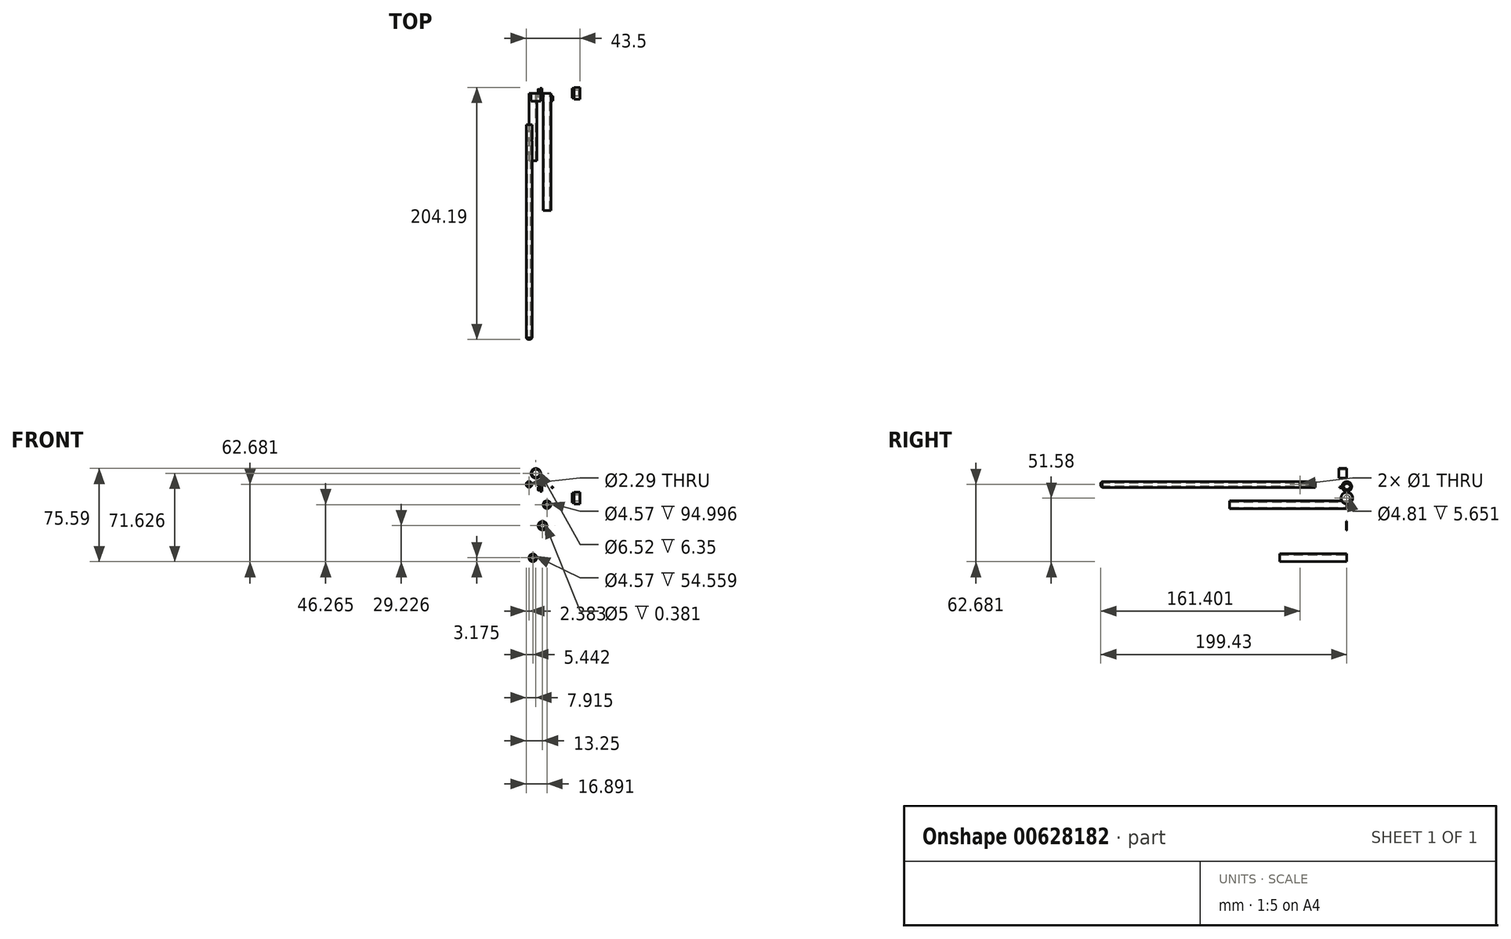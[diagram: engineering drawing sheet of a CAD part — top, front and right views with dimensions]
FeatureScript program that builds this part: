
annotation { "Feature Type Name" : "Feature", "Feature Type Description" : "" }
export const myFeature = defineFeature(function(context is Context, id is Id, definition is map)
    precondition{}
    {
        {
            var Q0;
            Q0=qCreatedBy(makeId("Front.planeOp"),FACE);
            var sketch = newSketch(context, id + "F0", { "sketchPlane" : qUnion([Q0])});
            skCircle(sketch, "E0", {"center": v(-51.91, 52.53) * mm, "radius": 3.97 * mm});
            skCircle(sketch, "E1", {"center": v(-51.91, 52.53) * mm, "radius": 3.26 * mm});
            skSolve(sketch);
        }
        {
            var Q0;
            Q0=makeQuery(id+"F0.imprint","IMPRINT",FACE,{"disambiguationData":[TD([[makeQuery(id+"F0.imprint","IMPRINT",EDGE,{"derivedFrom":sQuery(id+"F0.wireOp",EDGE,"E0")}),1.0]])]});
            extrude(context, id + "F1", {"entities" : qUnion([Q0]), "depth" : 6.35 * mm});
        }
        {
            var Q0;
            Q0=qCreatedBy(makeId("Front.planeOp"),FACE);
            var sketch = newSketch(context, id + "F2", { "sketchPlane" : qUnion([Q0])});
            skCircle(sketch, "E2", {"center": v(-64.02, 41.15) * mm, "radius": 0.5 * mm});
            skSolve(sketch);
        }
        {
            var Q0;
            Q0=makeQuery(id+"F2.imprint","IMPRINT",FACE,{"disambiguationData":[TD([[makeQuery(id+"F2.imprint","IMPRINT",EDGE,{"derivedFrom":sQuery(id+"F2.wireOp",EDGE,"E2")}),1.0]])]});
            extrude(context, id + "F3", {"entities" : qUnion([Q0]), "depth" : 6 * mm});
        }
        {
            var Q0;
            Q0=qCreatedBy(makeId("Front.planeOp"),FACE);
            var sketch = newSketch(context, id + "F4", { "sketchPlane" : qUnion([Q0])});
            skCircle(sketch, "E3", {"center": v(-57.45, 43.58) * mm, "radius": 1.14 * mm});
            skCircle(sketch, "E4", {"center": v(-57.45, 43.58) * mm, "radius": 2.38 * mm});
            skSolve(sketch);
        }
        {
            var Q0;
            Q0=makeQuery(id+"F4.imprint","IMPRINT",FACE,{"disambiguationData":[TD([[makeQuery(id+"F4.imprint","IMPRINT",EDGE,{"derivedFrom":sQuery(id+"F4.wireOp",EDGE,"E3")}),-1.0]])]});
            extrude(context, id + "F5", {"entities" : qUnion([Q0]), "depth" : 169.06 * mm + 5 * mm});
        }
        {
            var Q0;
            Q0=qCreatedBy(makeId("Front.planeOp"),FACE);
            var sketch = newSketch(context, id + "F6", { "sketchPlane" : qUnion([Q0])});
            skLineSegment(sketch, "E5.left", {"start": v(-50.2, 41.88) * mm, "end": v(-50.2, 45.11) * mm});
            skLineSegment(sketch, "E6.bottom", {"start": v(-48.6, 45.85) * mm, "end": v(-47.02, 45.85) * mm});
            skLineSegment(sketch, "E6.top", {"start": v(-48.6, 45.85) * mm, "end": v(-47.02, 45.85) * mm});
            skLineSegment(sketch, "E6.left", {"start": v(-50.2, 45.85) * mm, "end": v(-50.2, 45.85) * mm});
            skLineSegment(sketch, "E6.right", {"start": v(-47.02, 45.85) * mm, "end": v(-47.02, 45.85) * mm});
            skLineSegment(sketch, "E7.top", {"start": v(-47.02, 44.38) * mm, "end": v(-47.02, 44.38) * mm});
            skLineSegment(sketch, "E7.left", {"start": v(-47.02, 45.85) * mm, "end": v(-47.02, 44.38) * mm});
            skLineSegment(sketch, "E7.right", {"start": v(-47.02, 45.85) * mm, "end": v(-47.02, 44.38) * mm});
            skLineSegment(sketch, "E8.right", {"start": v(-44.58, 44.38) * mm, "end": v(-44.58, 44.38) * mm});
            skLineSegment(sketch, "E9.bottom", {"start": v(-50.2, 41.88) * mm, "end": v(-47.02, 41.88) * mm});
            skLineSegment(sketch, "E9.left", {"start": v(-50.2, 41.88) * mm, "end": v(-50.2, 41.86) * mm});
            skLineSegment(sketch, "E10", {"start": v(-47.02, 44.38) * mm, "end": v(-47.02, 41.88) * mm});
            skLineSegment(sketch, "E11", {"start": v(-48.6, 45.85) * mm, "end": v(-48.6, 45.11) * mm});
            skPoint(sketch, "E11.endSnap0", {"position": v(-47.02, 45.11) * mm});
            skLineSegment(sketch, "E12", {"start": v(-48.6, 45.11) * mm, "end": v(-50.2, 45.11) * mm});
            skSolve(sketch);
        }
        {
            var Q0;
            Q0=makeQuery(id+"F3.opExtrude","SWEPT_BODY",BODY,{"disambiguationData":[OSD([sQuery(id+"F2.wireOp",EDGE,"E2")])]});
            var Q1;
            Q1=qCreatedBy(makeId("Right.planeOp"),FACE);
            transform(context, id + "F7", {"entities" : qUnion([Q0]), "transformType" : TransformType.TRANSLATION_DISTANCE, "transformDirection" : qUnion([Q1]), "distance" : 25.4 * mm, "makeCopy" : false});
        }
        {
            var Q0;
            Q0=makeQuery(id+"F5.opExtrude","SWEPT_BODY",BODY,{"disambiguationData":[OSD([sQuery(id+"F4.wireOp",EDGE,"E3"),sQuery(id+"F4.wireOp",EDGE,"E4")])]});
            transform(context, id + "F8", {"entities" : qUnion([Q0]), "transformType" : TransformType.TRANSLATION_3D, "dx" : 0 * mm, "dy" : -25.4 * mm, "dz" : 0 * mm, "makeCopy" : false});
        }
        {
            var Q0;
            Q0=makeQuery(id+"F6.imprint","IMPRINT",FACE,{"disambiguationData":[TD([[makeQuery(id+"F6.imprint","IMPRINT",EDGE,{"derivedFrom":sQuery(id+"F6.wireOp",EDGE,"E5.left")}),-1.0]])]});
            var Q1;
            Q1=sQuery(id+"F6.wireOp",EDGE,"E9.bottom");
            revolve(context, id + "F9", {"entities" : qUnion([Q0]), "axis" : qUnion([Q1]), "revolveType" : RevolveType.FULL});
        }
        {
            var Q0;
            Q0=makeQuery(id+"F9.opRevolve","SWEPT_FACE",FACE,{"disambiguationData":[OSD([sQuery(id+"F6.wireOp",EDGE,"E5.left")])]});
            var sketch = newSketch(context, id + "F10", { "sketchPlane" : qUnion([Q0])});
            skLineSegment(sketch, "E13", {"start": v(0, 47.63) * mm, "end": v(0, 37.86) * mm, "construction": true});
            skPoint(sketch, "E14.visualSharp", {"position": v(5.58, 45.21) * mm});
            skCircle(sketch, "E15.0.0", {"center": v(0, 41.88) * mm, "radius": 3.97 * mm});
            skLineSegment(sketch, "E16", {"start": v(-3.97, 41.88) * mm, "end": v(3.97, 41.88) * mm, "construction": true});
            skLineSegment(sketch, "E17", {"start": v(-0.6, 45.4) * mm, "end": v(0, 45.4) * mm});
            skLineSegment(sketch, "E18", {"start": v(-0.6, 45.4) * mm, "end": v(-0.6, 41.88) * mm});
            skLineSegment(sketch, "E19.MirrorCS", {"start": v(0.6, 45.4) * mm, "end": v(0.6, 41.88) * mm});
            skLineSegment(sketch, "E20.MirrorCS", {"start": v(0.6, 45.4) * mm, "end": v(0, 45.4) * mm});
            skLineSegment(sketch, "E21.MirrorCS", {"start": v(-0.6, 38.36) * mm, "end": v(-0.6, 41.88) * mm});
            skLineSegment(sketch, "E22.MirrorCS", {"start": v(0.6, 38.36) * mm, "end": v(0.6, 41.88) * mm});
            skLineSegment(sketch, "E23.MirrorCS", {"start": v(0.6, 38.36) * mm, "end": v(0, 38.36) * mm});
            skLineSegment(sketch, "E24.MirrorCS", {"start": v(-0.6, 38.36) * mm, "end": v(0, 38.36) * mm});
            skSolve(sketch);
        }
        {
            var Q0;
            {var subQ6=sQuery(id+"F10.wireOp",EDGE,"E21.MirrorCS");var subQ8=sQuery(id+"F10.wireOp",EDGE,"E18");var subQ9=makeQuery(id+"F10.imprint","INTERSECT",VERTEX,{"derivedFrom":[subQ8,subQ6]});Q0=makeQuery(id+"F10.imprint","IMPRINT",FACE,{"disambiguationData":[TD([[makeQuery(id+"F10.imprint","IMPRINT",EDGE,{"disambiguationData":[TD([[subQ9,1.0]])],"derivedFrom":subQ8}),1.0]])]});}
            var Q1;
            {var subQ5=sQuery(id+"F10.wireOp",EDGE,"E17");Q1=makeQuery(id+"F10.imprint","IMPRINT",FACE,{"disambiguationData":[TD([[makeQuery(id+"F10.imprint","IMPRINT",EDGE,{"derivedFrom":subQ5}),-1.0]])]});}
            var Q2;
            {var subQ0=sQuery(id+"F10.wireOp",EDGE,"E23.MirrorCS");Q2=makeQuery(id+"F10.imprint","IMPRINT",FACE,{"disambiguationData":[TD([[makeQuery(id+"F10.imprint","IMPRINT",EDGE,{"derivedFrom":subQ0}),-1.0]])]});}
            var Q3;
            Q3=sQuery(id+"F10.wireOp",EDGE,"2e8Hojdz-Ffpt-K0kl-VxPV-xugqv5EDbXKW");
            var Q4;
            Q4=sQuery(id+"F10.wireOp",EDGE,"6102cfec-8d7d-461d-8d47-9e56d8466cac");
            var Q5;
            Q5=sQuery(id+"F10.wireOp",EDGE,"agnaYoGs-KZ4Y-nJwN-nZj2-FF0KZsyTTmNx");
            var Q6;
            Q6=sQuery(id+"F10.wireOp",EDGE,"wewaszXl-kRDa-fHt1-iyU0-6mpRW7kojRDx");
            var Q7;
            Q7=sQuery(id+"F10.wireOp",EDGE,"H97231xH-nEsN-Zyv9-0dKe-9AKgBbp31TFk");
            var Q8;
            Q8=sQuery(id+"F10.wireOp",EDGE,"9b957f26-6c3a-4b0b-aece-a967bed79c3a0.MirrorCS");
            extrude(context, id + "F11", {"entities" : qUnion([Q0, Q1, Q2]), "operationType" : NewBodyOperationType.REMOVE, "surfaceEntities" : qUnion([Q3, Q4, Q5, Q6, Q7, Q8]), "oppositeDirection" : true, "depth" : 1.59 * mm});
        }
        {
            var Q0;
            Q0=makeQuery(id+"F11.boolean.opBoolean","SPLIT",FACE,{"disambiguationData":[TD([makeQuery(id+"F11.opExtrude","SWEPT_FACE",FACE,{"disambiguationData":[OSD([sQuery(id+"F10.wireOp",EDGE,"E19.MirrorCS"),sQuery(id+"F10.wireOp",EDGE,"E22.MirrorCS")])]})])],"derivedFrom":makeQuery(id+"F9.opRevolve","SWEPT_FACE",FACE,{"disambiguationData":[OSD([sQuery(id+"F6.wireOp",EDGE,"E5.left")])]})});
            var sketch = newSketch(context, id + "F12", { "sketchPlane" : qUnion([Q0])});
            skCircle(sketch, "E25", {"center": v(0, 41.83) * mm, "radius": 2.5 * mm});
            skSolve(sketch);
        }
        {
            var Q0;
            {var subQ0=sQuery(id+"F12.wireOp",EDGE,"E25");var subQ1=makeQuery(id+"F11.boolean.opBoolean","COPY",EDGE,{"derivedFrom":makeQuery(id+"F11.opExtrude","CAP_EDGE",EDGE,{"disambiguationData":[OSD([sQuery(id+"F10.wireOp",EDGE,"agnaYoGs-KZ4Y-nJwN-nZj2-FF0KZsyTTmNx"),sQuery(id+"F10.wireOp",EDGE,"wewaszXl-kRDa-fHt1-iyU0-6mpRW7kojRDx")])],"isStart":true})});var subQ2=makeQuery(id+"F12.imprint","INTERSECT",VERTEX,{"disambiguationData":[OD(0.0)],"derivedFrom":[subQ1,subQ0]});Q0=makeQuery(id+"F12.imprint","IMPRINT",FACE,{"disambiguationData":[TD([[makeQuery(id+"F12.imprint","IMPRINT",EDGE,{"disambiguationData":[TD([[subQ2,1.0]])],"derivedFrom":subQ0}),1.0]])]});}
            var Q1;
            {var subQ0=sQuery(id+"F12.wireOp",EDGE,"E25");var subQ1=makeQuery(id+"F11.boolean.opBoolean","COPY",EDGE,{"derivedFrom":makeQuery(id+"F11.opExtrude","CAP_EDGE",EDGE,{"disambiguationData":[OSD([sQuery(id+"F10.wireOp",EDGE,"2e8Hojdz-Ffpt-K0kl-VxPV-xugqv5EDbXKW"),sQuery(id+"F10.wireOp",EDGE,"H97231xH-nEsN-Zyv9-0dKe-9AKgBbp31TFk")])],"isStart":true})});var subQ2=makeQuery(id+"F12.imprint","INTERSECT",VERTEX,{"disambiguationData":[OD(0.0)],"derivedFrom":[subQ1,subQ0]});Q1=makeQuery(id+"F12.imprint","IMPRINT",FACE,{"disambiguationData":[TD([[makeQuery(id+"F12.imprint","IMPRINT",EDGE,{"disambiguationData":[TD([[subQ2,1.0]])],"derivedFrom":subQ0}),1.0]])]});}
            var Q2;
            {var subQ0=sQuery(id+"F12.wireOp",EDGE,"E25");var subQ1=makeQuery(id+"F11.boolean.opBoolean","COPY",EDGE,{"derivedFrom":makeQuery(id+"F11.opExtrude","CAP_EDGE",EDGE,{"disambiguationData":[OSD([sQuery(id+"F10.wireOp",EDGE,"2e8Hojdz-Ffpt-K0kl-VxPV-xugqv5EDbXKW"),sQuery(id+"F10.wireOp",EDGE,"H97231xH-nEsN-Zyv9-0dKe-9AKgBbp31TFk")])],"isStart":true})});var subQ2=makeQuery(id+"F12.imprint","INTERSECT",VERTEX,{"disambiguationData":[OD(0.0)],"derivedFrom":[subQ1,subQ0]});Q2=makeQuery(id+"F12.imprint","IMPRINT",FACE,{"disambiguationData":[TD([[makeQuery(id+"F12.imprint","IMPRINT",EDGE,{"disambiguationData":[TD([[subQ2,-1.0]])],"derivedFrom":subQ0}),1.0]])]});}
            extrude(context, id + "F13", {"entities" : qUnion([Q0, Q1, Q2]), "operationType" : NewBodyOperationType.REMOVE, "oppositeDirection" : true, "depth" : 25.4 * mm});
        }
        {
            var Q0;
            Q0=makeQuery(id+"F11.boolean.opBoolean","SPLIT",FACE,{"disambiguationData":[TD([makeQuery(id+"F11.opExtrude","SWEPT_FACE",FACE,{"disambiguationData":[OSD([sQuery(id+"F10.wireOp",EDGE,"E18"),sQuery(id+"F10.wireOp",EDGE,"E21.MirrorCS")])]})])],"derivedFrom":makeQuery(id+"F9.opRevolve","SWEPT_FACE",FACE,{"disambiguationData":[OSD([sQuery(id+"F6.wireOp",EDGE,"E5.left")])]})});
            var sketch = newSketch(context, id + "F14", { "sketchPlane" : qUnion([Q0])});
            skLineSegment(sketch, "E26", {"start": v(0, 45.85) * mm, "end": v(0, 37.91) * mm, "construction": true});
            skPoint(sketch, "E26.endSnap0", {"position": v(-4.1, 43.5) * mm});
            skLineSegment(sketch, "E27", {"start": v(-3.97, 41.83) * mm, "end": v(3.97, 41.83) * mm, "construction": true});
            skLineSegment(sketch, "E28", {"start": v(0, 41.23) * mm, "end": v(3.12, 41.23) * mm});
            skLineSegment(sketch, "E29", {"start": v(3.38, 41.48) * mm, "end": v(3.38, 41.83) * mm});
            skLineSegment(sketch, "E30", {"start": v(3.12, 41.23) * mm, "end": v(3.12, 41.23) * mm});
            skPoint(sketch, "E31.visualSharp", {"position": v(3.38, 41.23) * mm});
            skArc(sketch, "E31.filletArc", {"start": v(3.12, 41.23) * mm, "mid": v(3.3, 41.3) * mm, "end": v(3.38, 41.48) * mm});
            skLineSegment(sketch, "E32.MirrorCS", {"start": v(0, 42.43) * mm, "end": v(3.12, 42.43) * mm});
            skArc(sketch, "E33.MirrorCS", {"start": v(3.12, 42.43) * mm, "mid": v(3.3, 42.36) * mm, "end": v(3.38, 42.18) * mm});
            skLineSegment(sketch, "E34.MirrorCS", {"start": v(3.38, 42.18) * mm, "end": v(3.38, 41.83) * mm});
            skLineSegment(sketch, "E35.MirrorCS", {"start": v(0, 42.43) * mm, "end": v(-3.13, 42.43) * mm});
            skArc(sketch, "E36.MirrorCS", {"start": v(-3.13, 42.43) * mm, "mid": v(-3.3, 42.36) * mm, "end": v(-3.38, 42.18) * mm});
            skLineSegment(sketch, "E37.MirrorCS", {"start": v(-3.38, 42.18) * mm, "end": v(-3.38, 41.83) * mm});
            skLineSegment(sketch, "E38.MirrorCS", {"start": v(-3.38, 41.48) * mm, "end": v(-3.38, 41.83) * mm});
            skArc(sketch, "E39.MirrorCS", {"start": v(-3.13, 41.23) * mm, "mid": v(-3.3, 41.3) * mm, "end": v(-3.38, 41.48) * mm});
            skLineSegment(sketch, "E40.MirrorCS", {"start": v(0, 41.23) * mm, "end": v(-3.13, 41.23) * mm});
            skCircle(sketch, "E41.0", {"center": v(0, 41.88) * mm, "radius": 3.97 * mm});
            skSolve(sketch);
        }
        {
            var Q0;
            {var subQ2=sQuery(id+"F14.wireOp",EDGE,"E28");Q0=makeQuery(id+"F14.imprint","IMPRINT",FACE,{"disambiguationData":[TD([[makeQuery(id+"F14.imprint","IMPRINT",EDGE,{"derivedFrom":subQ2}),1.0]])]});}
            var Q1;
            {var subQ9=sQuery(id+"F14.wireOp",EDGE,"E36.MirrorCS");var subQ10=sQuery(id+"F14.wireOp",EDGE,"E35.MirrorCS");var subQ11=makeQuery(id+"F14.imprint","INTERSECT",VERTEX,{"derivedFrom":[subQ10,subQ9]});Q1=makeQuery(id+"F14.imprint","IMPRINT",FACE,{"disambiguationData":[TD([[makeQuery(id+"F14.imprint","IMPRINT",EDGE,{"disambiguationData":[TD([[subQ11,1.0]])],"derivedFrom":subQ10}),1.0]])]});}
            var Q2;
            {var subQ6=sQuery(id+"F14.wireOp",EDGE,"E37.MirrorCS");Q2=makeQuery(id+"F14.imprint","IMPRINT",FACE,{"disambiguationData":[TD([[makeQuery(id+"F14.imprint","IMPRINT",EDGE,{"derivedFrom":subQ6}),1.0]])]});}
            extrude(context, id + "F15", {"entities" : qUnion([Q0, Q1, Q2]), "operationType" : NewBodyOperationType.REMOVE, "oppositeDirection" : true, "depth" : 6.35 * mm});
        }
        {
            var Q0;
            Q0=makeQuery(id+"F13.boolean.opBoolean","SPLIT",EDGE,{"disambiguationData":[OD(1.0)],"derivedFrom":makeQuery(id+"F11.boolean.opBoolean","COPY",EDGE,{"derivedFrom":makeQuery(id+"F11.opExtrude","CAP_EDGE",EDGE,{"disambiguationData":[OSD([sQuery(id+"F10.wireOp",EDGE,"E18"),sQuery(id+"F10.wireOp",EDGE,"E21.MirrorCS")])],"isStart":true})})});
            var Q1;
            Q1=makeQuery(id+"F13.boolean.opBoolean","SPLIT",EDGE,{"disambiguationData":[OD(1.0)],"derivedFrom":makeQuery(id+"F11.boolean.opBoolean","COPY",EDGE,{"derivedFrom":makeQuery(id+"F11.opExtrude","CAP_EDGE",EDGE,{"disambiguationData":[OSD([sQuery(id+"F10.wireOp",EDGE,"E19.MirrorCS"),sQuery(id+"F10.wireOp",EDGE,"E22.MirrorCS")])],"isStart":true})})});
            var Q2;
            {var subQ0=sQuery(id+"F14.wireOp",EDGE,"E35.MirrorCS");var subQ1=sQuery(id+"F14.wireOp",EDGE,"E32.MirrorCS");Q2=makeQuery(id+"F15.boolean.opBoolean","COPY",EDGE,{"disambiguationData":[TD([makeQuery(id+"F15.opExtrude","SWEPT_FACE",FACE,{"disambiguationData":[OSD([sQuery(id+"F14.wireOp",EDGE,"E36.MirrorCS")])]})])],"derivedFrom":makeQuery(id+"F15.opExtrude","CAP_EDGE",EDGE,{"disambiguationData":[OSD([subQ1,subQ0])],"isStart":true})});}
            var Q3;
            Q3=makeQuery(id+"F15.boolean.opBoolean","COPY",EDGE,{"derivedFrom":makeQuery(id+"F15.opExtrude","CAP_EDGE",EDGE,{"disambiguationData":[OSD([sQuery(id+"F14.wireOp",EDGE,"E36.MirrorCS")])],"isStart":true})});
            var Q4;
            {var subQ0=sQuery(id+"F14.wireOp",EDGE,"E40.MirrorCS");var subQ1=sQuery(id+"F14.wireOp",EDGE,"E28");Q4=makeQuery(id+"F15.boolean.opBoolean","COPY",EDGE,{"disambiguationData":[TD([makeQuery(id+"F15.opExtrude","SWEPT_FACE",FACE,{"disambiguationData":[OSD([sQuery(id+"F14.wireOp",EDGE,"E39.MirrorCS")])]})])],"derivedFrom":makeQuery(id+"F15.opExtrude","CAP_EDGE",EDGE,{"disambiguationData":[OSD([subQ1,subQ0])],"isStart":true})});}
            var Q5;
            Q5=makeQuery(id+"F15.boolean.opBoolean","COPY",EDGE,{"derivedFrom":makeQuery(id+"F15.opExtrude","CAP_EDGE",EDGE,{"disambiguationData":[OSD([sQuery(id+"F14.wireOp",EDGE,"E39.MirrorCS")])],"isStart":true})});
            var Q6;
            Q6=makeQuery(id+"F13.boolean.opBoolean","SPLIT",EDGE,{"disambiguationData":[OD(0.0)],"derivedFrom":makeQuery(id+"F11.boolean.opBoolean","COPY",EDGE,{"derivedFrom":makeQuery(id+"F11.opExtrude","CAP_EDGE",EDGE,{"disambiguationData":[OSD([sQuery(id+"F10.wireOp",EDGE,"E18"),sQuery(id+"F10.wireOp",EDGE,"E21.MirrorCS")])],"isStart":true})})});
            var Q7;
            Q7=makeQuery(id+"F13.boolean.opBoolean","SPLIT",EDGE,{"disambiguationData":[OD(0.0)],"derivedFrom":makeQuery(id+"F11.boolean.opBoolean","COPY",EDGE,{"derivedFrom":makeQuery(id+"F11.opExtrude","CAP_EDGE",EDGE,{"disambiguationData":[OSD([sQuery(id+"F10.wireOp",EDGE,"E19.MirrorCS"),sQuery(id+"F10.wireOp",EDGE,"E22.MirrorCS")])],"isStart":true})})});
            var Q8;
            {var subQ0=sQuery(id+"F14.wireOp",EDGE,"E40.MirrorCS");var subQ1=sQuery(id+"F14.wireOp",EDGE,"E28");Q8=makeQuery(id+"F15.boolean.opBoolean","COPY",EDGE,{"disambiguationData":[TD([makeQuery(id+"F15.opExtrude","SWEPT_FACE",FACE,{"disambiguationData":[OSD([sQuery(id+"F14.wireOp",EDGE,"E31.filletArc")])]})])],"derivedFrom":makeQuery(id+"F15.opExtrude","CAP_EDGE",EDGE,{"disambiguationData":[OSD([subQ1,subQ0])],"isStart":true})});}
            var Q9;
            {var subQ0=sQuery(id+"F14.wireOp",EDGE,"E35.MirrorCS");var subQ1=sQuery(id+"F14.wireOp",EDGE,"E32.MirrorCS");Q9=makeQuery(id+"F15.boolean.opBoolean","COPY",EDGE,{"disambiguationData":[TD([makeQuery(id+"F15.opExtrude","SWEPT_FACE",FACE,{"disambiguationData":[OSD([sQuery(id+"F14.wireOp",EDGE,"E33.MirrorCS")])]})])],"derivedFrom":makeQuery(id+"F15.opExtrude","CAP_EDGE",EDGE,{"disambiguationData":[OSD([subQ1,subQ0])],"isStart":true})});}
            chamfer(context, id + "F16", {"entities" : qUnion([Q0, Q1, Q2, Q3, Q4, Q5, Q6, Q7, Q8, Q9]), "width" : 0.38 * mm, "tangentPropagation" : true});
        }
        {
            var Q0;
            Q0=qCreatedBy(makeId("Front.planeOp"),FACE);
            var sketch = newSketch(context, id + "F17", { "sketchPlane" : qUnion([Q0])});
            skCircle(sketch, "E42", {"center": v(-42.94, 27.17) * mm, "radius": 2.29 * mm});
            skCircle(sketch, "E43", {"center": v(-42.94, 27.17) * mm, "radius": 3.17 * mm});
            skSolve(sketch);
        }
        {
            var Q0;
            Q0=qSketchRegion(id+"F17",true);
            extrude(context, id + "F18", {"entities" : qUnion([Q0]), "depth" : 95 * mm});
        }
        {
            var Q0;
            Q0=qCreatedBy(makeId("Front.planeOp"),FACE);
            var sketch = newSketch(context, id + "F19", { "sketchPlane" : qUnion([Q0])});
            skLineSegment(sketch, "E44", {"start": v(-22.7, 32.48) * mm, "end": v(-8.46, 32.48) * mm, "construction": true});
            skLineSegment(sketch, "E45", {"start": v(-22.7, 34.89) * mm, "end": v(-22.7, 36.45) * mm});
            skLineSegment(sketch, "E46", {"start": v(-22.7, 36.45) * mm, "end": v(-21.1, 36.45) * mm});
            skLineSegment(sketch, "E47", {"start": v(-21.1, 36.45) * mm, "end": v(-21.1, 37.24) * mm});
            skLineSegment(sketch, "E48", {"start": v(-21.1, 37.24) * mm, "end": v(-16.33, 37.24) * mm});
            skLineSegment(sketch, "E49", {"start": v(-16.33, 37.24) * mm, "end": v(-16.33, 32.48) * mm});
            skLineSegment(sketch, "E50", {"start": v(-16.33, 32.48) * mm, "end": v(-17.04, 32.48) * mm});
            skLineSegment(sketch, "E51", {"start": v(-17.04, 32.48) * mm, "end": v(-17.04, 34.89) * mm});
            skLineSegment(sketch, "E52", {"start": v(-17.04, 34.89) * mm, "end": v(-22.7, 34.89) * mm});
            skSolve(sketch);
        }
        {
            var Q0;
            Q0=makeQuery(id+"F19.imprint","IMPRINT",FACE,{"disambiguationData":[TD([[makeQuery(id+"F19.imprint","IMPRINT",EDGE,{"derivedFrom":sQuery(id+"F19.wireOp",EDGE,"E45")}),-1.0]])]});
            var Q1;
            Q1=sQuery(id+"F19.wireOp",EDGE,"E44");
            revolve(context, id + "F20", {"entities" : qUnion([Q0]), "axis" : qUnion([Q1]), "revolveType" : RevolveType.FULL});
        }
        {
            var Q0;
            Q0=qCreatedBy(makeId("Front.planeOp"),FACE);
            var sketch = newSketch(context, id + "F21", { "sketchPlane" : qUnion([Q0])});
            skCircle(sketch, "E53", {"center": v(-46.58, 10.13) * mm, "radius": 2.5 * mm});
            skCircle(sketch, "E54", {"center": v(-46.58, 10.13) * mm, "radius": 3.56 * mm});
            skSolve(sketch);
        }
        {
            var Q0;
            Q0=makeQuery(id+"F21.imprint","IMPRINT",FACE,{"disambiguationData":[TD([[makeQuery(id+"F21.imprint","IMPRINT",EDGE,{"derivedFrom":sQuery(id+"F21.wireOp",EDGE,"E53")}),-1.0]])]});
            extrude(context, id + "F22", {"entities" : qUnion([Q0]), "depth" : 0.38 * mm});
        }
        {
            var Q0;
            Q0=qCreatedBy(makeId("Right.planeOp"),FACE);
            var sketch = newSketch(context, id + "F23", { "sketchPlane" : qUnion([Q0])});
            skLineSegment(sketch, "E55", {"start": v(-76.2, 45.96) * mm, "end": v(-25.4, 45.96) * mm});
            skLineSegment(sketch, "E56.0", {"start": v(-25.4, 41.2) * mm, "end": v(-25.4, 45.96) * mm});
            skLineSegment(sketch, "E57", {"start": v(-25.4, 41.2) * mm, "end": v(-76.2, 41.2) * mm});
            skCircle(sketch, "E58", {"center": v(-38.03, 43.58) * mm, "radius": 0.5 * mm});
            skPoint(sketch, "E58.centerSnap0", {"position": v(-25.4, 43.58) * mm});
            skLineSegment(sketch, "E59", {"start": v(-31.05, 41.2) * mm, "end": v(-31.05, 45.96) * mm, "construction": true});
            skLineSegment(sketch, "E60", {"start": v(-37.53, 41.2) * mm, "end": v(-37.53, 45.96) * mm, "construction": true});
            skLineSegment(sketch, "E61", {"start": v(-37.15, 45.96) * mm, "end": v(-37.15, 41.2) * mm, "construction": true});
            skSolve(sketch);
        }
        {
            var Q0;
            Q0=makeQuery(id+"F23.imprint","IMPRINT",FACE,{"disambiguationData":[TD([[makeQuery(id+"F23.imprint","IMPRINT",EDGE,{"derivedFrom":sQuery(id+"F23.wireOp",EDGE,"E58")}),1.0]])]});
            var Q1;
            Q1=makeQuery(id+"F5.opExtrude","SWEPT_FACE",FACE,{"disambiguationData":[OSD([sQuery(id+"F4.wireOp",EDGE,"E4")])]});
            var Q2;
            Q2=makeQuery(id+"F5.opExtrude","SWEPT_BODY",BODY,{"disambiguationData":[OSD([sQuery(id+"F4.wireOp",EDGE,"E3"),sQuery(id+"F4.wireOp",EDGE,"E4")])]});
            extrude(context, id + "F24", {"entities" : qUnion([Q0]), "operationType" : NewBodyOperationType.REMOVE, "endBound" : BoundingType.THROUGH_ALL, "oppositeDirection" : true, "endBoundEntityFace" : qUnion([Q1]), "endBoundEntityBody" : qUnion([Q2]), "depth" : 25.4 * mm});
        }
        {
            var Q0;
            Q0=qCreatedBy(makeId("Front.planeOp"),FACE);
            var sketch = newSketch(context, id + "F25", { "sketchPlane" : qUnion([Q0])});
            skCircle(sketch, "E62", {"center": v(-54.39, -15.92) * mm, "radius": 3.18 * mm});
            skCircle(sketch, "E63", {"center": v(-54.39, -15.92) * mm, "radius": 2.29 * mm});
            skSolve(sketch);
        }
        {
            var Q0;
            Q0=makeQuery(id+"F25.imprint","IMPRINT",FACE,{"disambiguationData":[TD([[makeQuery(id+"F25.imprint","IMPRINT",EDGE,{"derivedFrom":sQuery(id+"F25.wireOp",EDGE,"E62")}),1.0]])]});
            extrude(context, id + "F26", {"entities" : qUnion([Q0]), "depth" : 54.56 * mm});
        }
        {
            var Q0;
            Q0=makeQuery(id+"F5.opExtrude","CAP_EDGE",EDGE,{"disambiguationData":[OSD([sQuery(id+"F4.wireOp",EDGE,"E4")])],"isStart":false});
            chamfer(context, id + "F27", {"entities" : qUnion([Q0]), "width" : 1.27 * mm, "tangentPropagation" : true});
        }
    });
